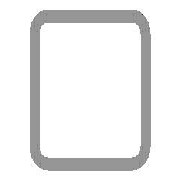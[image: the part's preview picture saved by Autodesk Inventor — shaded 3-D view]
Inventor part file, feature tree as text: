
AUTODESK INVENTOR PART (.ipt)
format: ipt  version: 2025 (Build 290162010, 162A)  size: 132,608 bytes
history: native  units: mm (DEFAULTED — no unit token found)
features: other x4, sketch x1, plane x1
ambient origin geometry x8: Origin, YZ Plane, XZ Plane, XY Plane, X Axis, Y Axis, Z Axis, Center Point
bodies: Solid1 (feature_tree), Body (feature_tree)
feature tree (6):
  parser-record x1  (decoder bookkeeping rows leaked as tree rows — omitted from the tree; the rows remain in map.json)
  other  "Driven Length"
  other  "Start Plane"
  other  "End Plane"
  sketch  "Sketch3"  dims[d3=1250.0mm d4=0.0mm d7=4.0mm d9=40.0mm d11=40.0mm d12=2.0mm d13=-0.0mm d14=1250.0mm d15=20.0mm d16=20.0mm d17=90.0deg d18=1250.0mm]
  plane  "Work Plane3"
